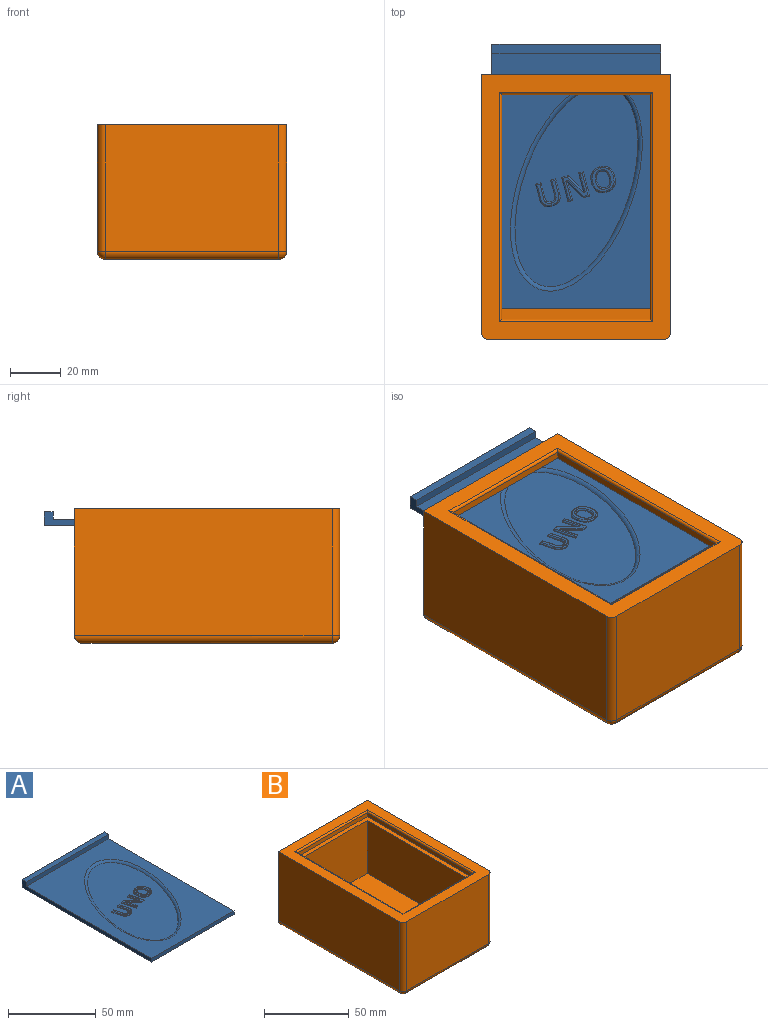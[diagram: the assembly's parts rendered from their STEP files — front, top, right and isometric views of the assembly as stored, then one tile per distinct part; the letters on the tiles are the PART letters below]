
ASSEMBLY  parts=2 mates=1
PART A: 100 faces, bbox 66.5x104.3x5.5 mm
  f0: plane 104.25x5.5mm, normal (-1,0,0), area 271.1mm2, adj f1,f3,f4,f5,f6,f7
  f1: plane 66.5x2.5mm, normal (0,-1,0), area 166.3mm2, adj f0,f2,f3,f4
  f2: plane 104.25x5.5mm, normal (1,0,0), area 271.1mm2, adj f1,f3,f4,f5,f6,f7
  f3: plane 104.25x66.5mm, normal (0,0,-1), area 6932.6mm2, adj f0,f1,f2,f6
  f4: plane 100.75x66.5mm, normal (0,0,1), area 3625.1mm2, adj f0,f1,f2,f5,f99
  f5: plane 66.5x3mm, normal (0,-1,0), area 199.5mm2, adj f0,f2,f4,f7
  f6: plane 66.5x5.5mm, normal (0,1,0), area 365.7mm2, adj f0,f2,f3,f7
  f7: plane 66.5x3.5mm, normal (0,0,1), area 232.8mm2, adj f0,f2,f5,f6
  f8: plane 79.04x48.44mm, normal (0,0,1), area 2536.6mm2, adj f9,f10,f11,f12,f13,f14,f15,f16
  f9: plane 2.03x0.53mm, normal (-0.25,0.97,0), area 0.5mm2, adj f8,f10,f23,f97
  f10: plane 5.86x1.52mm, normal (-0.97,-0.25,0), area 1.5mm2, adj f8,f9,f11,f98
  f11: extruded ~1.75x0.25mm, area 0.4mm2, adj f8,f10,f12,f96
  f12: extruded ~1.31x0.9mm, area 0.4mm2, adj f8,f11,f13,f94
  f13: extruded ~1.61x0.25mm, area 0.4mm2, adj f8,f12,f14,f92
  f14: extruded ~1.51x0.87mm, area 0.4mm2, adj f8,f13,f15,f90
  f15: plane 5.87x1.53mm, normal (0.97,0.25,0), area 1.5mm2, adj f8,f14,f16,f88
  f16: plane 2.03x0.53mm, normal (-0.25,0.97,0), area 0.5mm2, adj f8,f15,f17,f86
  f17: plane 6.18x1.61mm, normal (-0.97,-0.25,0), area 1.6mm2, adj f8,f16,f18,f84
  f18: extruded ~2.33x1.7mm, area 0.7mm2, adj f8,f17,f19,f85
  f19: extruded ~3.12x0.4mm, area 0.8mm2, adj f8,f18,f20,f87
  f20: extruded ~2.02x0.98mm, area 0.6mm2, adj f8,f19,f21,f89
  f21: extruded ~1.59x1.06mm, area 0.5mm2, adj f8,f20,f22,f91
  f22: extruded ~1.99x0.25mm, area 0.5mm2, adj f8,f21,f23,f93
  f23: plane 6.21x1.61mm, normal (0.97,0.25,0), area 1.6mm2, adj f8,f9,f22,f95
  f24: plane 9.86x8.52mm, normal (0,0,1), area 21.8mm2, adj f84,f85,f86,f87,f88,f89,f90,f91
  f25: plane 9.6x2.5mm, normal (0.97,0.25,0), area 2.5mm2, adj f8,f26,f38,f79
  f26: plane 1.83x0.48mm, normal (-0.25,0.97,0), area 0.5mm2, adj f8,f25,f27,f77
  f27: plane 4.54x1.18mm, normal (-0.97,-0.25,0), area 1.2mm2, adj f8,f26,f28,f75
  f28: extruded ~2.62x0.79mm, area 0.7mm2, adj f8,f27,f29,f73
  f29: plane 0.25x0.05mm, normal (-0.25,0.97,0), area 0mm2, adj f8,f28,f30,f71
  f30: plane 6.1x6.04mm, normal (0.71,0.7,0), area 2.1mm2, adj f8,f29,f31,f70
  f31: plane 2.57x0.67mm, normal (-0.25,0.97,0), area 0.7mm2, adj f8,f30,f32,f72
  f32: plane 9.6x2.5mm, normal (-0.97,-0.25,0), area 2.5mm2, adj f8,f31,f33,f74
  f33: plane 1.82x0.47mm, normal (0.25,-0.97,0), area 0.5mm2, adj f8,f32,f34,f76
  f34: plane 4.52x1.17mm, normal (0.97,0.25,0), area 1.2mm2, adj f8,f33,f35,f78
  f35: extruded ~2.71x0.84mm, area 0.7mm2, adj f8,f34,f36,f80
  f36: plane 0.25x0.06mm, normal (0.25,-0.97,0), area 0mm2, adj f8,f35,f37,f82
  f37: plane 6.17x6.06mm, normal (-0.71,-0.7,0), area 2.2mm2, adj f8,f36,f38,f83
  f38: plane 2.59x0.67mm, normal (0.25,-0.97,0), area 0.7mm2, adj f8,f25,f37,f81
  f39: plane 10.59x9.79mm, normal (0,0,1), area 26.1mm2, adj f70,f71,f72,f73,f74,f75,f76,f77
  f40: extruded ~3.36x2.12mm, area 1mm2, adj f8,f41,f53,f68
  f41: extruded ~3.72x0.61mm, area 1mm2, adj f8,f40,f42,f69
  f42: extruded ~3.07x2.15mm, area 1mm2, adj f8,f41,f43,f67
  f43: extruded ~3.97x0.5mm, area 1mm2, adj f8,f42,f44,f65
  f44: extruded ~3.37x2.14mm, area 1mm2, adj f8,f43,f45,f63
  f45: extruded ~3.72x0.61mm, area 1mm2, adj f8,f44,f46,f62
  f46: extruded ~3.05x2.16mm, area 1mm2, adj f8,f45,f53,f64
  f47: extruded ~2.58x0.25mm, area 0.7mm2, adj f48,f52,f55,f60
  f48: extruded ~1.62x1.29mm, area 0.5mm2, adj f47,f49,f55,f61
  f49: extruded ~3.26x2.71mm, area 1.2mm2, adj f48,f50,f55,f59
  f50: extruded ~3.87x1.81mm, area 1.2mm2, adj f49,f51,f55,f57
  f51: extruded ~2.04x0.44mm, area 0.5mm2, adj f50,f52,f55,f56
  f52: extruded ~2.26x1.24mm, area 0.7mm2, adj f47,f51,f55,f58
  f53: extruded ~3.97x0.49mm, area 1mm2, adj f8,f40,f46,f66
  f54: plane 9.32x8.67mm, normal (0,0,1), area 26.1mm2, adj f56,f57,f58,f59,f60,f61,f62,f63
  f55: plane 7.14x5.79mm, normal (0,0,1), area 28mm2, adj f47,f48,f49,f50,f51,f52
  f56: bspline ~3.4x1.27mm, area 1.8mm2, adj f51,f54,f57,f58
  f57: bspline ~5.84x3.39mm, area 4mm2, adj f50,f54,f56,f59
  f58: bspline ~3.61x2.35mm, area 2.2mm2, adj f52,f54,f56,f60
  f59: bspline ~5.24x4.3mm, area 4mm2, adj f49,f54,f57,f61
  f60: bspline ~4.03x0.93mm, area 2.2mm2, adj f47,f54,f58,f61
  f61: bspline ~2.65x2.02mm, area 1.8mm2, adj f48,f54,f59,f60
  f62: bspline ~5.5x1.39mm, area 2.9mm2, adj f45,f54,f63,f64
  f63: bspline ~5.46x3.47mm, area 3.1mm2, adj f44,f54,f62,f65
  f64: bspline ~4.72x3.28mm, area 2.9mm2, adj f46,f54,f62,f66
  f65: bspline ~6.16x1.31mm, area 3.1mm2, adj f43,f54,f63,f67
  f66: bspline ~6.19x1.31mm, area 3.1mm2, adj f53,f54,f64,f68
  f67: bspline ~4.53x2.86mm, area 2.9mm2, adj f42,f54,f65,f69
  f68: bspline ~5.44x3.46mm, area 3.1mm2, adj f40,f54,f66,f69
  f69: bspline ~5.49x1.38mm, area 2.9mm2, adj f41,f54,f67,f68
  f70: cylinder r=0.5mm len=6.66mm, axis (0.7,-0.71,0), area 6.7mm2, adj f30,f39,f71,f72
  f71: cylinder r=0.5mm len=0.96mm, axis (0.97,0.25,0), area 0.3mm2, adj f29,f39,f70,f73
  f72: cylinder r=0.5mm len=2.69mm, axis (0.97,0.25,0), area 1.8mm2, adj f31,f39,f70,f74
  f73: bspline ~5.83x2.22mm, area 2.3mm2, adj f28,f39,f71,f75
  f74: cylinder r=0.5mm len=9.72mm, axis (-0.25,0.97,0), area 7.4mm2, adj f32,f39,f72,f76
  f75: cylinder r=0.5mm len=4.67mm, axis (-0.25,0.97,0), area 3.5mm2, adj f27,f39,f73,f77
  f76: cylinder r=0.5mm len=1.94mm, axis (-0.97,-0.25,0), area 1.1mm2, adj f33,f39,f74,f78
  f77: cylinder r=0.5mm len=1.96mm, axis (0.97,0.25,0), area 1.1mm2, adj f26,f39,f75,f79
  f78: cylinder r=0.5mm len=4.64mm, axis (0.25,-0.97,0), area 3.5mm2, adj f34,f39,f76,f80
  f79: cylinder r=0.5mm len=9.72mm, axis (0.25,-0.97,0), area 7.4mm2, adj f25,f39,f77,f81
  f80: bspline ~5.98x2.33mm, area 2.4mm2, adj f35,f39,f78,f82
  f81: cylinder r=0.5mm len=2.71mm, axis (-0.97,-0.25,0), area 1.8mm2, adj f38,f39,f79,f83
  f82: cylinder r=0.5mm len=0.98mm, axis (-0.97,-0.25,0), area 0.3mm2, adj f36,f39,f80,f83
  f83: cylinder r=0.5mm len=6.73mm, axis (-0.7,0.71,0), area 6.8mm2, adj f37,f39,f81,f82
  f84: cylinder r=0.5mm len=6.31mm, axis (-0.25,0.97,0), area 4.8mm2, adj f17,f24,f85,f86
  f85: bspline ~3.82x3mm, area 2.2mm2, adj f18,f24,f84,f87
  f86: cylinder r=0.5mm len=2.15mm, axis (0.97,0.25,0), area 1.3mm2, adj f16,f24,f84,f88
  f87: bspline ~4.8x1.13mm, area 2.4mm2, adj f19,f24,f85,f89
  f88: cylinder r=0.5mm len=6mm, axis (0.25,-0.97,0), area 4.6mm2, adj f15,f24,f86,f90
  f89: bspline ~2.95x1.78mm, area 1.7mm2, adj f20,f24,f87,f91
  f90: bspline ~2.76x1.8mm, area 1.5mm2, adj f14,f24,f88,f92
  f91: bspline ~2.36x1.79mm, area 1.4mm2, adj f21,f24,f89,f93
  f92: bspline ~2.83x1mm, area 1.4mm2, adj f13,f24,f90,f94
  f93: bspline ~2.5x0.73mm, area 1.5mm2, adj f22,f24,f91,f95
  f94: bspline ~2.37x1.88mm, area 1.4mm2, adj f12,f24,f92,f96
  f95: cylinder r=0.5mm len=6.33mm, axis (0.25,-0.97,0), area 4.8mm2, adj f23,f24,f93,f97
  f96: bspline ~3.06x0.81mm, area 1.5mm2, adj f11,f24,f94,f98
  f97: cylinder r=0.5mm len=2.15mm, axis (0.97,0.25,0), area 1.3mm2, adj f9,f24,f95,f98
  f98: cylinder r=0.5mm len=5.99mm, axis (-0.25,0.97,0), area 4.6mm2, adj f10,f24,f96,f97
  f99: bspline ~82.39x51.86mm, area 431.4mm2, adj f4,f8
PART B: 32 faces, bbox 74.5x104.5x53 mm
  f0: plane 74.5x50mm, normal (0,1,0), area 3538mm2, adj f1,f2,f4,f10,f11,f12,f13,f23
  f1: plane 101.5x50mm, normal (1,0,0), area 5075mm2, adj f0,f4,f20,f21
  f2: plane 101.5x50mm, normal (-1,0,0), area 5075mm2, adj f0,f4,f25,f27
  f3: plane 68.5x50mm, normal (0,-1,0), area 3425mm2, adj f4,f20,f24,f27
  f4: plane 104.5x74.5mm, normal (0,0,1), area 2306.1mm2, adj f0,f1,f2,f3,f20,f27,f28,f29
  f5: plane 98.5x68.5mm, normal (0,0,-1), area 6747.3mm2, adj f21,f23,f24,f25
  f6: plane 88.5x2.85mm, normal (-1,0,0), area 252.2mm2, adj f7,f9,f13,f31
  f7: plane 58.5x2.85mm, normal (0,-1,0), area 166.7mm2, adj f6,f8,f13,f30
  f8: plane 88.5x2.85mm, normal (1,0,0), area 252.2mm2, adj f7,f9,f13,f28
  f9: plane 58.5x2.85mm, normal (0,1,0), area 166.7mm2, adj f6,f8,f13,f29
  f10: plane 100.65x2.8mm, normal (1,0,0), area 281.8mm2, adj f0,f12,f13,f14
  f11: plane 100.65x2.8mm, normal (-1,0,0), area 281.8mm2, adj f0,f12,f13,f14
  f12: plane 100.65x66.8mm, normal (0,0,1), area 1546.2mm2, adj f0,f10,f11,f14,f16,f17,f18,f19
  f13: plane 100.65x66.8mm, normal (0,0,-1), area 1546.2mm2, adj f0,f6,f7,f8,f9,f10,f11,f14
  f14: plane 66.8x2.8mm, normal (0,1,0), area 187mm2, adj f10,f11,f12,f13
  f15: plane 88.5x58.5mm, normal (0,0,1), area 5177.2mm2, adj f16,f17,f18,f19
  f16: plane 58.5x38.35mm, normal (0,1,0), area 2243.5mm2, adj f12,f15,f17,f19
  f17: plane 88.5x38.35mm, normal (1,0,0), area 3394mm2, adj f12,f15,f16,f18
  f18: plane 58.5x38.35mm, normal (0,-1,0), area 2243.5mm2, adj f12,f15,f17,f19
  f19: plane 88.5x38.35mm, normal (-1,0,0), area 3394mm2, adj f12,f15,f16,f18
  f20: cylinder r=3mm len=50mm, axis (0,0,1), area 235.6mm2, adj f1,f3,f4,f22
  f21: cylinder r=3mm len=101.5mm, axis (0,1,0), area 473.2mm2, adj f1,f5,f22,f23
  f22: sphere r=3mm, area 14.1mm2, adj f20,f21,f24
  f23: cylinder r=3mm len=74.5mm, axis (-1,0,0), area 340.8mm2, adj f0,f5,f21,f25
  f24: cylinder r=3mm len=68.5mm, axis (1,0,0), area 322.8mm2, adj f3,f5,f22,f26
  f25: cylinder r=3mm len=101.5mm, axis (0,-1,0), area 473.2mm2, adj f2,f5,f23,f26
  f26: sphere r=3mm, area 14.1mm2, adj f24,f25,f27
  f27: cylinder r=3mm len=50mm, axis (0,0,-1), area 235.6mm2, adj f2,f3,f4,f26
  f28: cylinder r=1mm len=90.5mm, axis (0,-1,0), area 140.2mm2, adj f4,f8,f29,f30
  f29: cylinder r=1mm len=60.5mm, axis (1,0,0), area 93mm2, adj f4,f9,f28,f31
  f30: cylinder r=1mm len=60.5mm, axis (-1,0,0), area 93mm2, adj f4,f7,f28,f31
  f31: cylinder r=1mm len=90.5mm, axis (0,1,0), area 140.2mm2, adj f4,f6,f29,f30
PLACE A t=(1.36,7.67,-2.34)mm
PLACE B t=(1.21,-0.43,-2.19)mm
MATE slider B.f0 <-> A.f6  axis (0,1,0) through (34.61,51.82,36.16)mm
